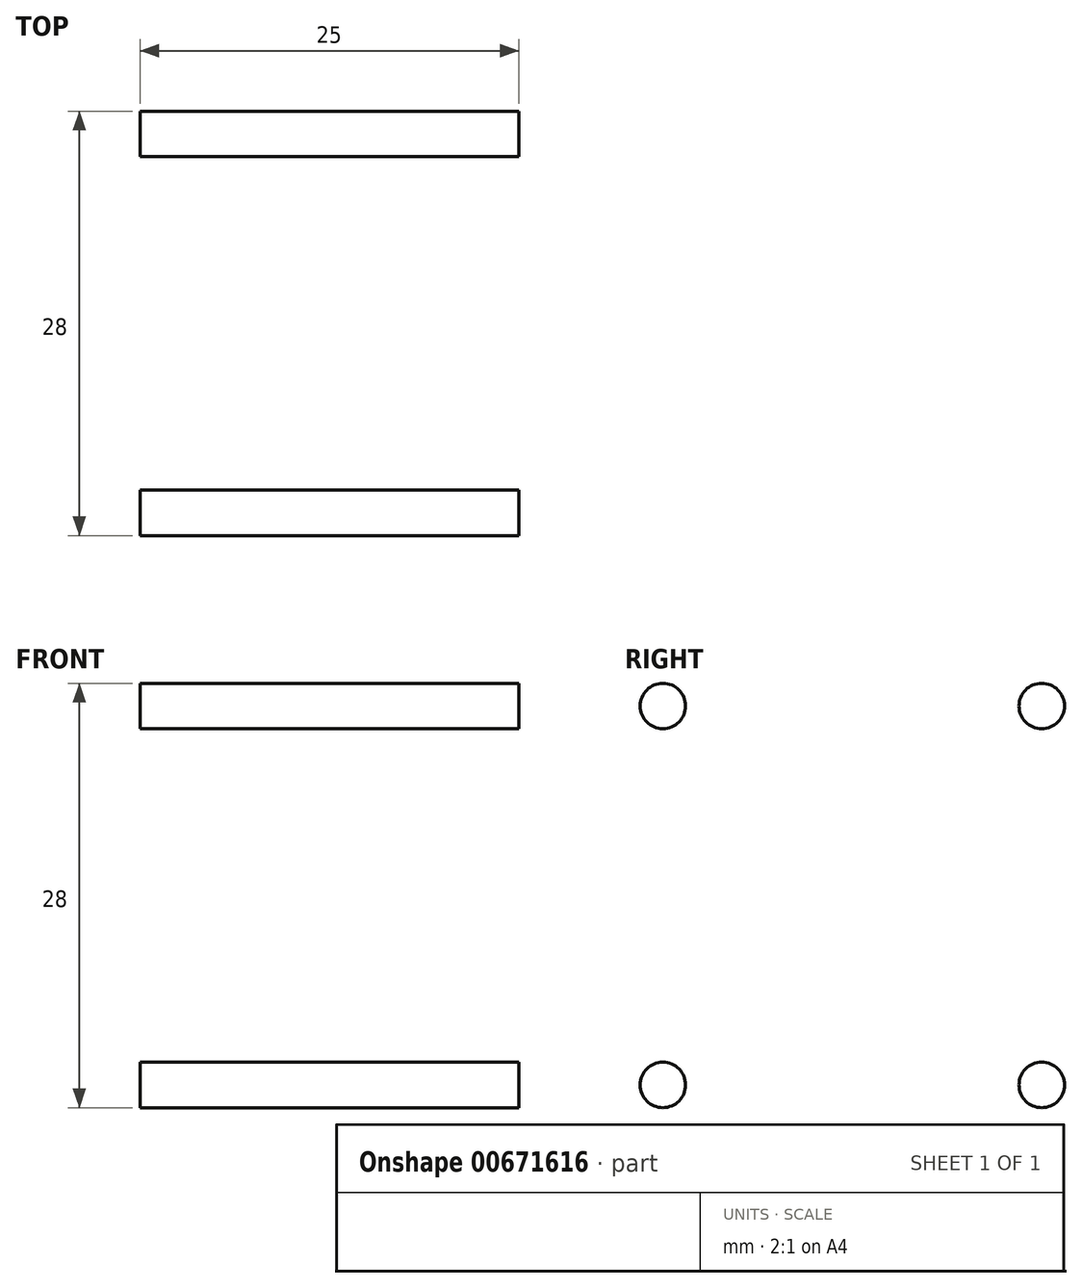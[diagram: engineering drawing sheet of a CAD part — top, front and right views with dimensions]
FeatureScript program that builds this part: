
annotation { "Feature Type Name" : "Feature", "Feature Type Description" : "" }
export const myFeature = defineFeature(function(context is Context, id is Id, definition is map)
    precondition{}
    {
        {
            var Q0;
            Q0=qCreatedBy(makeId("Right.planeOp"),FACE);
            var sketch = newSketch(context, id + "F0", { "sketchPlane" : qUnion([Q0])});
            skCircle(sketch, "E0", {"center": v(-12.5, 12.5) * mm, "radius": 1.5 * mm});
            skCircle(sketch, "E1.0.1.0", {"center": v(-12.5, -12.5) * mm, "radius": 1.5 * mm});
            skCircle(sketch, "E1.1.0.0", {"center": v(12.5, 12.5) * mm, "radius": 1.5 * mm});
            skCircle(sketch, "E1.1.1.0", {"center": v(12.5, -12.5) * mm, "radius": 1.5 * mm});
            skLineSegment(sketch, "E1.direction1", {"start": v(-12.5, 12.5) * mm, "end": v(12.5, 12.5) * mm, "construction": true});
            skLineSegment(sketch, "E1.direction2", {"start": v(-12.5, 12.5) * mm, "end": v(-12.5, -12.5) * mm, "construction": true});
            skLineSegment(sketch, "E2", {"start": v(12.5, 12.5) * mm, "end": v(-12.5, -12.5) * mm, "construction": true});
            skSolve(sketch);
        }
        {
            var Q0;
            Q0=makeQuery(id+"F0.imprint","IMPRINT",FACE,{"disambiguationData":[TD([[makeQuery(id+"F0.imprint","IMPRINT",EDGE,{"derivedFrom":sQuery(id+"F0.wireOp",EDGE,"E1.1.0.0")}),1.0]])]});
            var Q1;
            Q1=makeQuery(id+"F0.imprint","IMPRINT",FACE,{"disambiguationData":[TD([[makeQuery(id+"F0.imprint","IMPRINT",EDGE,{"derivedFrom":sQuery(id+"F0.wireOp",EDGE,"E1.1.1.0")}),1.0]])]});
            var Q2;
            Q2=makeQuery(id+"F0.imprint","IMPRINT",FACE,{"disambiguationData":[TD([[makeQuery(id+"F0.imprint","IMPRINT",EDGE,{"derivedFrom":sQuery(id+"F0.wireOp",EDGE,"E1.0.1.0")}),1.0]])]});
            var Q3;
            Q3=makeQuery(id+"F0.imprint","IMPRINT",FACE,{"disambiguationData":[TD([[makeQuery(id+"F0.imprint","IMPRINT",EDGE,{"derivedFrom":sQuery(id+"F0.wireOp",EDGE,"E0")}),1.0]])]});
            var Q4;
            Q4=sQuery(id+"F0.wireOp",EDGE,"E0");
            var Q5;
            Q5=sQuery(id+"F0.wireOp",EDGE,"E1.1.0.0");
            var Q6;
            Q6=sQuery(id+"F0.wireOp",EDGE,"E1.1.1.0");
            var Q7;
            Q7=sQuery(id+"F0.wireOp",EDGE,"E1.0.1.0");
            extrude(context, id + "F1", {"entities" : qUnion([Q0, Q1, Q2, Q3]), "surfaceEntities" : qUnion([Q4, Q5, Q6, Q7]), "endBound" : BoundingType.SYMMETRIC, "depth" : 25 * mm, "offsetDistance" : 25 * mm});
        }
    });
